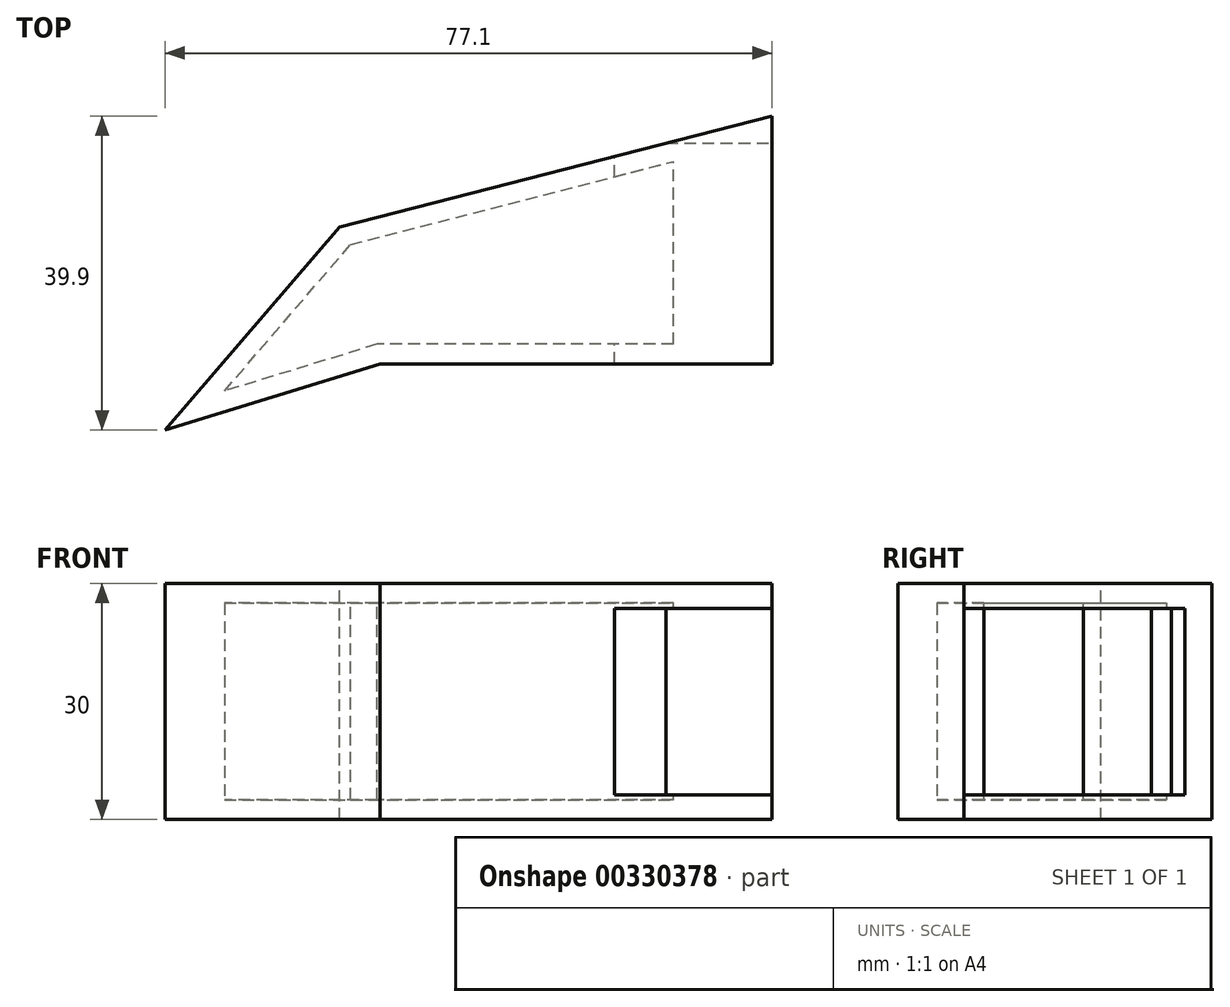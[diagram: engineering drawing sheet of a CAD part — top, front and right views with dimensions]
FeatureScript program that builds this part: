
annotation { "Feature Type Name" : "Feature", "Feature Type Description" : "" }
export const myFeature = defineFeature(function(context is Context, id is Id, definition is map)
    precondition{}
    {
        {
            var Q0;
            Q0=qCreatedBy(makeId("Top.planeOp"),FACE);
            var sketch = newSketch(context, id + "F0", { "sketchPlane" : qUnion([Q0])});
            skLineSegment(sketch, "E0.bottom", {"start": v(-48.3, 29.25) * mm, "end": v(28.8, 29.25) * mm});
            skLineSegment(sketch, "E0.top", {"start": v(-48.3, -10.65) * mm, "end": v(28.8, -10.65) * mm});
            skLineSegment(sketch, "E0.left", {"start": v(-48.3, 29.25) * mm, "end": v(-48.3, -10.65) * mm});
            skLineSegment(sketch, "E0.right", {"start": v(28.8, 29.25) * mm, "end": v(28.8, -10.65) * mm});
            skSolve(sketch);
        }
        {
            var Q0;
            Q0=makeQuery(id+"F0.imprint","IMPRINT",FACE,{"disambiguationData":[TD([[makeQuery(id+"F0.imprint","IMPRINT",EDGE,{"derivedFrom":sQuery(id+"F0.wireOp",EDGE,"E0.bottom")}),-1.0]])]});
            extrude(context, id + "F1", {"entities" : qUnion([Q0]), "depth" : 30 * mm});
        }
        {
            var Q0;
            Q0=makeQuery(id+"F1.opExtrude","CAP_FACE",FACE,{"disambiguationData":[OSD([sQuery(id+"F0.wireOp",EDGE,"E0.bottom"),sQuery(id+"F0.wireOp",EDGE,"E0.top"),sQuery(id+"F0.wireOp",EDGE,"E0.left"),sQuery(id+"F0.wireOp",EDGE,"E0.right")])],"isStart":false});
            var sketch = newSketch(context, id + "F2", { "sketchPlane" : qUnion([Q0])});
            skLineSegment(sketch, "E1", {"start": v(-48.3, -10.65) * mm, "end": v(-26.1, 15.15) * mm});
            skLineSegment(sketch, "E2", {"start": v(-26.1, 15.15) * mm, "end": v(28.8, 29.25) * mm});
            skLineSegment(sketch, "E3", {"start": v(28.8, 29.25) * mm, "end": v(28.8, -2.25) * mm});
            skLineSegment(sketch, "E4", {"start": v(28.8, -2.25) * mm, "end": v(-21, -2.25) * mm});
            skLineSegment(sketch, "E5", {"start": v(-21, -2.25) * mm, "end": v(-48.3, -10.65) * mm});
            skSolve(sketch);
        }
        {
            var Q0;
            Q0=makeQuery(id+"F2.imprint","IMPRINT",FACE,{"disambiguationData":[TD([[makeQuery(id+"F2.imprint","IMPRINT",EDGE,{"derivedFrom":sQuery(id+"F2.wireOp",EDGE,"E1")}),1.0]])]});
            var Q1;
            {var subQ0=sQuery(id+"F2.wireOp",EDGE,"E4");Q1=makeQuery(id+"F2.imprint","IMPRINT",FACE,{"disambiguationData":[TD([[makeQuery(id+"F2.imprint","IMPRINT",EDGE,{"derivedFrom":subQ0}),1.0]])]});}
            extrude(context, id + "F3", {"entities" : qUnion([Q0, Q1]), "operationType" : NewBodyOperationType.REMOVE, "endBound" : BoundingType.THROUGH_ALL, "oppositeDirection" : true, "depth" : 25 * mm});
        }
        {
            var Q0;
            Q0=makeQuery(id+"F1.opExtrude","SWEPT_FACE",FACE,{"disambiguationData":[OSD([sQuery(id+"F0.wireOp",EDGE,"E0.right")])]});
            var sketch = newSketch(context, id + "F4", { "sketchPlane" : qUnion([Q0])});
            skLineSegment(sketch, "E6.bottom", {"start": v(-2.25, 26.85) * mm, "end": v(25.8, 26.85) * mm});
            skLineSegment(sketch, "E6.top", {"start": v(-2.25, 3.15) * mm, "end": v(25.8, 3.15) * mm});
            skLineSegment(sketch, "E6.left", {"start": v(-2.25, 26.85) * mm, "end": v(-2.25, 3.15) * mm});
            skLineSegment(sketch, "E6.right", {"start": v(25.8, 26.85) * mm, "end": v(25.8, 3.15) * mm});
            skSolve(sketch);
        }
        {
            var Q0;
            Q0=makeQuery(id+"F4.imprint","IMPRINT",FACE,{"disambiguationData":[TD([[makeQuery(id+"F4.imprint","IMPRINT",EDGE,{"derivedFrom":sQuery(id+"F4.wireOp",EDGE,"E6.bottom")}),-1.0]])]});
            extrude(context, id + "F5", {"entities" : qUnion([Q0]), "operationType" : NewBodyOperationType.REMOVE, "oppositeDirection" : true, "depth" : 10 * mm});
        }
        {
            var Q0;
            Q0=makeQuery(id+"F1.opExtrude","CAP_FACE",FACE,{"disambiguationData":[OSD([sQuery(id+"F0.wireOp",EDGE,"E0.bottom"),sQuery(id+"F0.wireOp",EDGE,"E0.top"),sQuery(id+"F0.wireOp",EDGE,"E0.left"),sQuery(id+"F0.wireOp",EDGE,"E0.right")])],"isStart":true});
            var Q1;
            Q1=makeQuery(id+"F5.boolean.opBoolean","COPY",FACE,{"derivedFrom":makeQuery(id+"F5.opExtrude","CAP_FACE",FACE,{"disambiguationData":[OSD([sQuery(id+"F4.wireOp",EDGE,"E6.bottom"),sQuery(id+"F4.wireOp",EDGE,"E6.top"),sQuery(id+"F4.wireOp",EDGE,"E6.left"),sQuery(id+"F4.wireOp",EDGE,"E6.right")])],"isStart":false})});
            var Q2;
            Q2=makeQuery(id+"F3.boolean.opBoolean","COPY",FACE,{"derivedFrom":makeQuery(id+"F3.opExtrude","SWEPT_FACE",FACE,{"disambiguationData":[OSD([sQuery(id+"F2.wireOp",EDGE,"E1")])]})});
            var Q3;
            Q3=makeQuery(id+"F3.boolean.opBoolean","COPY",FACE,{"derivedFrom":makeQuery(id+"F3.opExtrude","SWEPT_FACE",FACE,{"disambiguationData":[OSD([sQuery(id+"F2.wireOp",EDGE,"E2")])]})});
            var Q4;
            Q4=makeQuery(id+"F5.boolean.opBoolean","COPY",FACE,{"derivedFrom":makeQuery(id+"F5.opExtrude","SWEPT_FACE",FACE,{"disambiguationData":[OSD([sQuery(id+"F4.wireOp",EDGE,"E6.right")])]})});
            var Q5;
            Q5=makeQuery(id+"F5.boolean.opBoolean","COPY",FACE,{"derivedFrom":makeQuery(id+"F5.opExtrude","SWEPT_FACE",FACE,{"disambiguationData":[OSD([sQuery(id+"F4.wireOp",EDGE,"E6.top")])]})});
            var Q6;
            Q6=makeQuery(id+"F3.boolean.opBoolean","COPY",FACE,{"derivedFrom":makeQuery(id+"F3.opExtrude","SWEPT_FACE",FACE,{"disambiguationData":[OSD([sQuery(id+"F2.wireOp",EDGE,"E5")])]})});
            var Q7;
            Q7=makeQuery(id+"F5.boolean.opBoolean","COPY",FACE,{"derivedFrom":makeQuery(id+"F5.opExtrude","SWEPT_FACE",FACE,{"disambiguationData":[OSD([sQuery(id+"F4.wireOp",EDGE,"E6.bottom")])]})});
            var Q8;
            Q8=makeQuery(id+"F1.opExtrude","SWEPT_FACE",FACE,{"disambiguationData":[OSD([sQuery(id+"F0.wireOp",EDGE,"E0.right")])]});
            var Q9;
            Q9=makeQuery(id+"F3.boolean.opBoolean","COPY",FACE,{"derivedFrom":makeQuery(id+"F3.opExtrude","SWEPT_FACE",FACE,{"disambiguationData":[OSD([sQuery(id+"F2.wireOp",EDGE,"E4")])]})});
            var Q10;
            Q10=makeQuery(id+"F1.opExtrude","SWEPT_BODY",BODY,{"disambiguationData":[OSD([sQuery(id+"F0.wireOp",EDGE,"E0.bottom"),sQuery(id+"F0.wireOp",EDGE,"E0.top"),sQuery(id+"F0.wireOp",EDGE,"E0.left"),sQuery(id+"F0.wireOp",EDGE,"E0.right")])]});
            shell(context, id + "F6", {"isHollow" : true, "entities" : qUnion([Q0, Q1, Q2, Q3, Q4, Q5, Q6, Q7, Q8, Q9]), "parts" : qUnion([Q10]), "thickness" : 2.5 * mm});
        }
        {
            var Q0;
            Q0=makeQuery(id+"F5.boolean.opBoolean","COPY",FACE,{"derivedFrom":makeQuery(id+"F5.opExtrude","CAP_FACE",FACE,{"disambiguationData":[OSD([sQuery(id+"F4.wireOp",EDGE,"E6.bottom"),sQuery(id+"F4.wireOp",EDGE,"E6.top"),sQuery(id+"F4.wireOp",EDGE,"E6.left"),sQuery(id+"F4.wireOp",EDGE,"E6.right")])],"isStart":false})});
            extrude(context, id + "F7", {"entities" : qUnion([Q0]), "operationType" : NewBodyOperationType.REMOVE, "oppositeDirection" : true, "depth" : 10 * mm});
        }
    });
